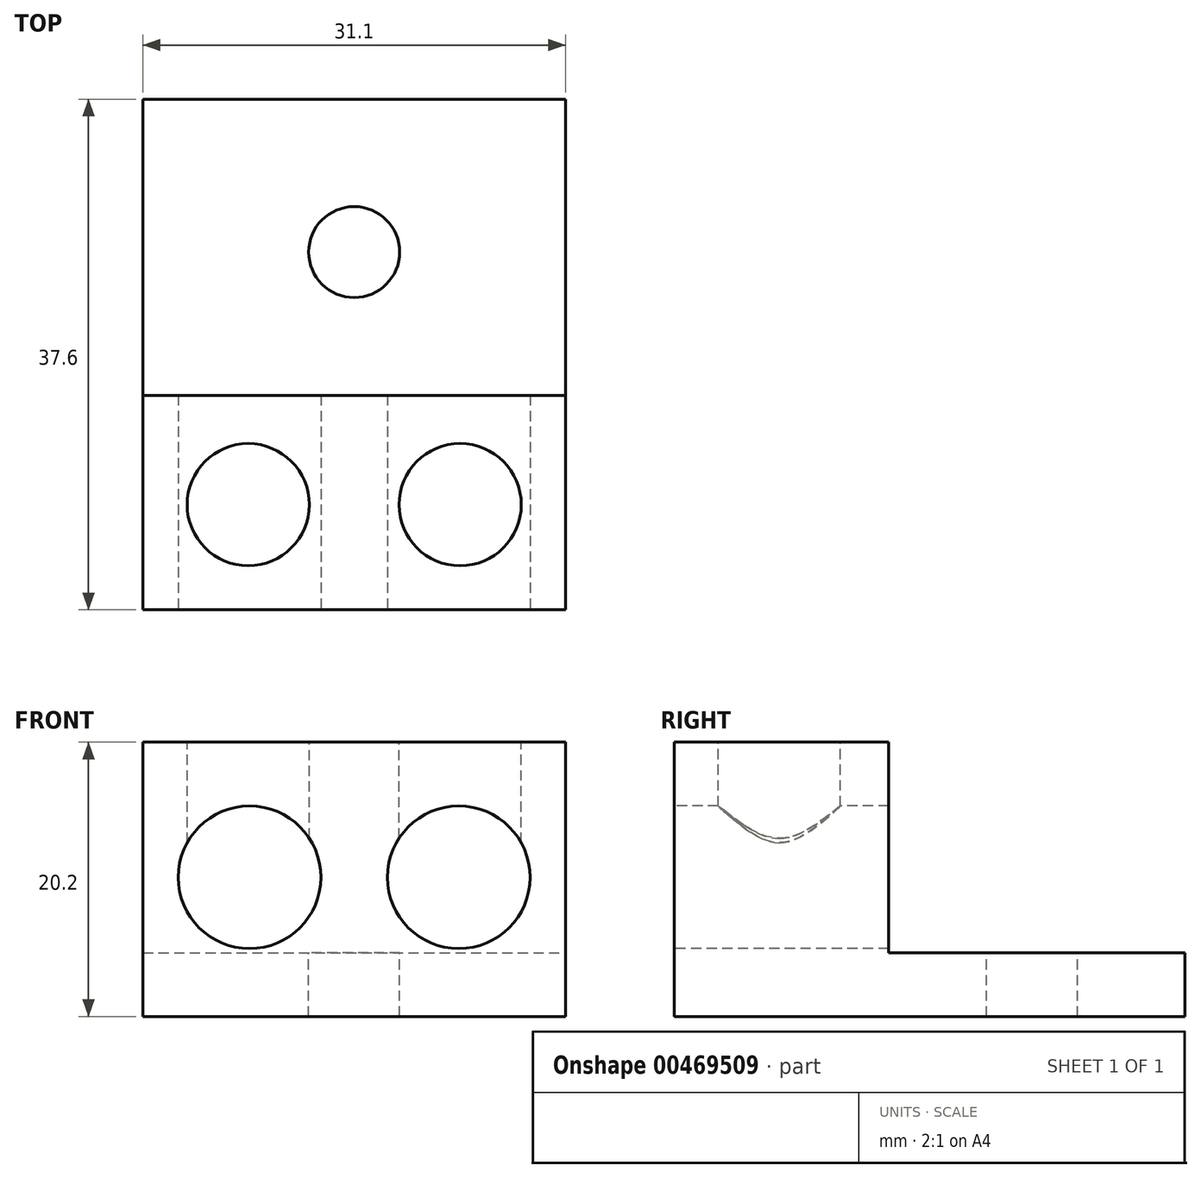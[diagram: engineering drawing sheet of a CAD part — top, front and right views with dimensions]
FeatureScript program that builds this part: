
annotation { "Feature Type Name" : "Feature", "Feature Type Description" : "" }
export const myFeature = defineFeature(function(context is Context, id is Id, definition is map)
    precondition{}
    {
        {
            var Q0;
            Q0=qCreatedBy(makeId("Top.planeOp"),FACE);
            var sketch = newSketch(context, id + "F0", { "sketchPlane" : qUnion([Q0])});
            skLineSegment(sketch, "E0.bottom", {"start": v(0, 0) * mm, "end": v(31.1, 0) * mm});
            skLineSegment(sketch, "E0.top", {"start": v(0, 37.6) * mm, "end": v(31.1, 37.6) * mm});
            skLineSegment(sketch, "E0.left", {"start": v(0, 0) * mm, "end": v(0, 37.6) * mm});
            skLineSegment(sketch, "E0.right", {"start": v(31.1, 0) * mm, "end": v(31.1, 37.6) * mm});
            skLineSegment(sketch, "E1.top", {"start": v(0, 15.8) * mm, "end": v(31.1, 15.8) * mm});
            skLineSegment(sketch, "E1.left", {"start": v(0, 0) * mm, "end": v(0, 15.8) * mm});
            skLineSegment(sketch, "E1.right", {"start": v(31.1, 0) * mm, "end": v(31.1, 15.8) * mm});
            skSolve(sketch);
        }
        {
            var Q0;
            Q0=makeQuery(id+"F0.imprint","IMPRINT",FACE,{"disambiguationData":[TD([[makeQuery(id+"F0.imprint","IMPRINT",EDGE,{"derivedFrom":sQuery(id+"F0.wireOp",EDGE,"E0.bottom")}),1.0]])]});
            extrude(context, id + "F1", {"entities" : qUnion([Q0]), "depth" : 20.2 * mm});
        }
        {
            var Q0;
            Q0 = qSketchRegion(id + "F0", true);
            extrude(context, id + "F2", {"entities" : qUnion([Q0]), "operationType" : NewBodyOperationType.ADD, "depth" : 4.7 * mm});
        }
        {
            var Q0;
            Q0=makeQuery(id+"F1.opExtrude","SWEPT_FACE",FACE,{"disambiguationData":[OSD([sQuery(id+"F0.wireOp",EDGE,"E0.bottom")])]});
            var sketch = newSketch(context, id + "F3", { "sketchPlane" : qUnion([Q0])});
            skCircle(sketch, "E2", {"center": v(7.85, 10.25) * mm, "radius": 5.25 * mm});
            skCircle(sketch, "E3", {"center": v(23.25, 10.25) * mm, "radius": 5.25 * mm});
            skSolve(sketch);
        }
        {
            var Q0;
            Q0 = qSketchRegion(id + "F3", true);
            extrude(context, id + "F4", {"entities" : qUnion([Q0]), "operationType" : NewBodyOperationType.REMOVE, "endBound" : BoundingType.THROUGH_ALL, "oppositeDirection" : true, "depth" : 25 * mm});
        }
        {
            var Q0;
            Q0=makeQuery(id+"F2.opExtrude","CAP_FACE",FACE,{"disambiguationData":[OSD([sQuery(id+"F0.wireOp",EDGE,"E0.top"),sQuery(id+"F0.wireOp",EDGE,"E0.left"),sQuery(id+"F0.wireOp",EDGE,"E0.right"),sQuery(id+"F0.wireOp",EDGE,"E0.bottom"),sQuery(id+"F0.wireOp",EDGE,"E1.left"),sQuery(id+"F0.wireOp",EDGE,"E1.right")])],"isStart":false});
            var sketch = newSketch(context, id + "F5", { "sketchPlane" : qUnion([Q0])});
            skCircle(sketch, "E4", {"center": v(15.55, 26.35) * mm, "radius": 3.35 * mm});
            skSolve(sketch);
        }
        {
            var Q0;
            Q0=makeQuery(id+"F5.imprint","IMPRINT",FACE,{"disambiguationData":[TD([[makeQuery(id+"F5.imprint","IMPRINT",EDGE,{"derivedFrom":sQuery(id+"F5.wireOp",EDGE,"E4")}),1.0]])]});
            extrude(context, id + "F6", {"entities" : qUnion([Q0]), "operationType" : NewBodyOperationType.REMOVE, "endBound" : BoundingType.THROUGH_ALL, "oppositeDirection" : true, "depth" : 25 * mm});
        }
        {
            var Q0;
            Q0=makeQuery(id+"F1.opExtrude","CAP_FACE",FACE,{"disambiguationData":[OSD([sQuery(id+"F0.wireOp",EDGE,"E0.bottom"),sQuery(id+"F0.wireOp",EDGE,"E1.top"),sQuery(id+"F0.wireOp",EDGE,"E1.left"),sQuery(id+"F0.wireOp",EDGE,"E1.right")])],"isStart":false});
            var sketch = newSketch(context, id + "F7", { "sketchPlane" : qUnion([Q0])});
            skCircle(sketch, "E5", {"center": v(7.75, 7.75) * mm, "radius": 4.5 * mm});
            skCircle(sketch, "E6", {"center": v(23.35, 7.75) * mm, "radius": 4.5 * mm});
            skSolve(sketch);
        }
        {
            var Q0;
            Q0=makeQuery(id+"F7.imprint","IMPRINT",FACE,{"disambiguationData":[TD([[makeQuery(id+"F7.imprint","IMPRINT",EDGE,{"derivedFrom":sQuery(id+"F7.wireOp",EDGE,"E5")}),1.0]])]});
            var Q1;
            Q1=makeQuery(id+"F7.imprint","IMPRINT",FACE,{"disambiguationData":[TD([[makeQuery(id+"F7.imprint","IMPRINT",EDGE,{"derivedFrom":sQuery(id+"F7.wireOp",EDGE,"E6")}),1.0]])]});
            extrude(context, id + "F8", {"entities" : qUnion([Q0, Q1]), "operationType" : NewBodyOperationType.REMOVE, "oppositeDirection" : true, "depth" : 9 * mm});
        }
    });
